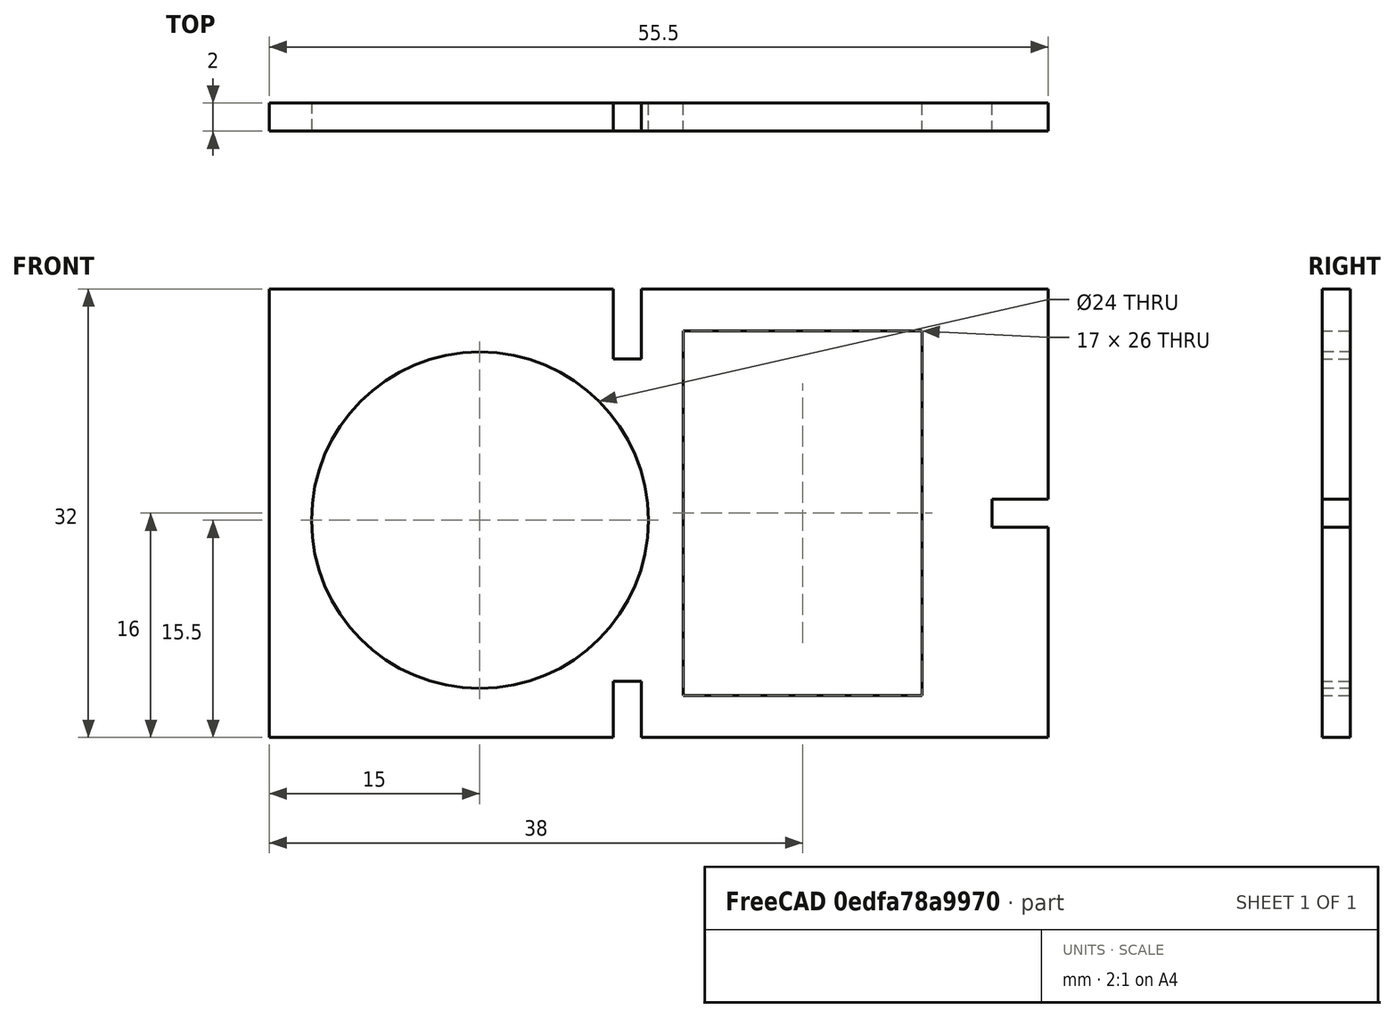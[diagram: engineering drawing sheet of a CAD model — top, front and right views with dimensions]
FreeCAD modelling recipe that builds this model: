
FCSTD DOCUMENT  (FreeCAD 0.14R3700 (Git))
Label: BIRR_fixMoteurAr
License: CC-BY 3.0
LicenseURL: http://creativecommons.org/licenses/by/3.0/
objects: Sketcher::SketchObject×1, Part::Extrusion×1, Part::Feature×1
note: 3 computed .brp shape members not serialized (recipe doc carries the construction recipe); baked Part::Feature solids carry a one-line shape summary decoded from their .brp

FEATURE [Sketcher::SketchObject] Sketch  label="fixMoteurAr"
  Placement = pos=(0,0,0) rot=(1,0,0;1.5708rad)
  sketch-geometry (21):
    g0: Circle CenterX=-12.75 CenterY=15.5 CenterZ=0 NormalX=0 NormalY=0 NormalZ=1 Radius=12
    g1: LineSegment StartX=1.75 StartY=29 StartZ=0 EndX=18.75 EndY=29 EndZ=0
    g2: LineSegment StartX=18.75 StartY=29 StartZ=0 EndX=18.75 EndY=3 EndZ=0
    g3: LineSegment StartX=18.75 StartY=3 StartZ=0 EndX=1.75 EndY=3 EndZ=0
    g4: LineSegment StartX=1.75 StartY=3 StartZ=0 EndX=1.75 EndY=29 EndZ=0
    g5: LineSegment StartX=-27.75 StartY=32 StartZ=0 EndX=-27.75 EndY=0 EndZ=0
    g6: LineSegment StartX=-27.75 StartY=32 StartZ=0 EndX=-3.25 EndY=32 EndZ=0
    g7: LineSegment StartX=-3.25 StartY=32 StartZ=0 EndX=-3.25 EndY=27 EndZ=0
    g8: LineSegment StartX=-3.25 StartY=27 StartZ=0 EndX=-1.25 EndY=27 EndZ=0
    g9: LineSegment StartX=-1.25 StartY=27 StartZ=0 EndX=-1.25 EndY=32 EndZ=0
    g10: LineSegment StartX=-1.25 StartY=32 StartZ=0 EndX=27.75 EndY=32 EndZ=0
    g11: LineSegment StartX=-27.75 StartY=0 StartZ=0 EndX=-3.25 EndY=0 EndZ=0
    g12: LineSegment StartX=-3.25 StartY=0 StartZ=0 EndX=-3.25 EndY=4 EndZ=0
    g13: LineSegment StartX=-3.25 StartY=4 StartZ=0 EndX=-1.25 EndY=4 EndZ=0
    g14: LineSegment StartX=-1.25 StartY=4 StartZ=0 EndX=-1.25 EndY=0 EndZ=0
    g15: LineSegment StartX=27.75 StartY=0 StartZ=0 EndX=-1.25 EndY=0 EndZ=0
    g16: LineSegment StartX=27.75 StartY=17 StartZ=0 EndX=23.75 EndY=17 EndZ=0
    g17: LineSegment StartX=23.75 StartY=17 StartZ=0 EndX=23.75 EndY=15 EndZ=0
    g18: LineSegment StartX=23.75 StartY=15 StartZ=0 EndX=27.75 EndY=15 EndZ=0
    g19: LineSegment StartX=27.75 StartY=32 StartZ=0 EndX=27.75 EndY=17 EndZ=0
    g20: LineSegment StartX=27.75 StartY=0 StartZ=0 EndX=27.75 EndY=15 EndZ=0
  constraints (62):
    c: Coincident(g1,g2)
    c: Coincident(g2,g3)
    c: Coincident(g3,g4)
    c: Coincident(g4,g1)
    c: Horizontal(g1)
    c: Horizontal(g3)
    c: Vertical(g2)
    c: Vertical(g4)
    c: Vertical(g5)
    c: PointOnObject(g5,g-1)
    c: Symmetric(g5,g15,g-2)
    c: DistanceY(g15,g2) = 3
    c: DistanceX(g3) = -17
    c: Radius(g0) = 12
    c: DistanceY(g2) = -26
    c: DistanceY(g1,g10) = 3
    c: DistanceY(g5,g0) = 15.5
    c: DistanceX(g0,g1) = 14.5
    c: DistanceX(g0,g5) = -15
    c: Coincident(g6,g5)
    c: Horizontal(g6)
    c: Coincident(g7,g6)
    c: Vertical(g7)
    c: Coincident(g8,g7)
    c: Horizontal(g8)
    c: Coincident(g9,g8)
    c: Vertical(g9)
    c: Coincident(g10,g9)
    c: Horizontal(g10)
    c: DistanceY(g7) = -5
    c: Coincident(g11,g5)
    c: Horizontal(g11)
    c: Coincident(g12,g11)
    c: Vertical(g12)
    c: Coincident(g13,g12)
    c: Coincident(g14,g13)
    c: Vertical(g14)
    c: Coincident(g15,g14)
    c: Horizontal(g15)
    c: DistanceY(g12) = 4
    c: Horizontal(g13)
    c: Coincident(g16,g17)
    c: Coincident(g17,g18)
    c: Horizontal(g16)
    c: Horizontal(g18)
    c: Vertical(g17)
    c: Coincident(g19,g10)
    c: Coincident(g19,g16)
    c: Vertical(g19)
    c: Coincident(g20,g15)
    c: Coincident(g20,g18)
    c: Vertical(g20)
    c: DistanceX(g18) = 4
    c: PointOnObject(g6,g10)
    c: DistanceY(g17) = -2
    c: PointOnObject(g16,g20)
    c: Equal(g19,g20)
    c: PointOnObject(g8,g14)
    c: DistanceX(g5,g10) = 55.5
    c: PointOnObject(g7,g12)
    c: DistanceX(g8,g1) = 3
    c: DistanceX(g11,g14) = 2
FEATURE [Part::Extrusion] Extrude001
  Base = -> Sketch
  Dir = (0,2,0)
  Solid = true
FEATURE [Part::Feature] Extrude001001  label="fixMoteurAr_copy"
  shape: bbox 55.5 x 2 x 32 mm, 23 faces (baked)
